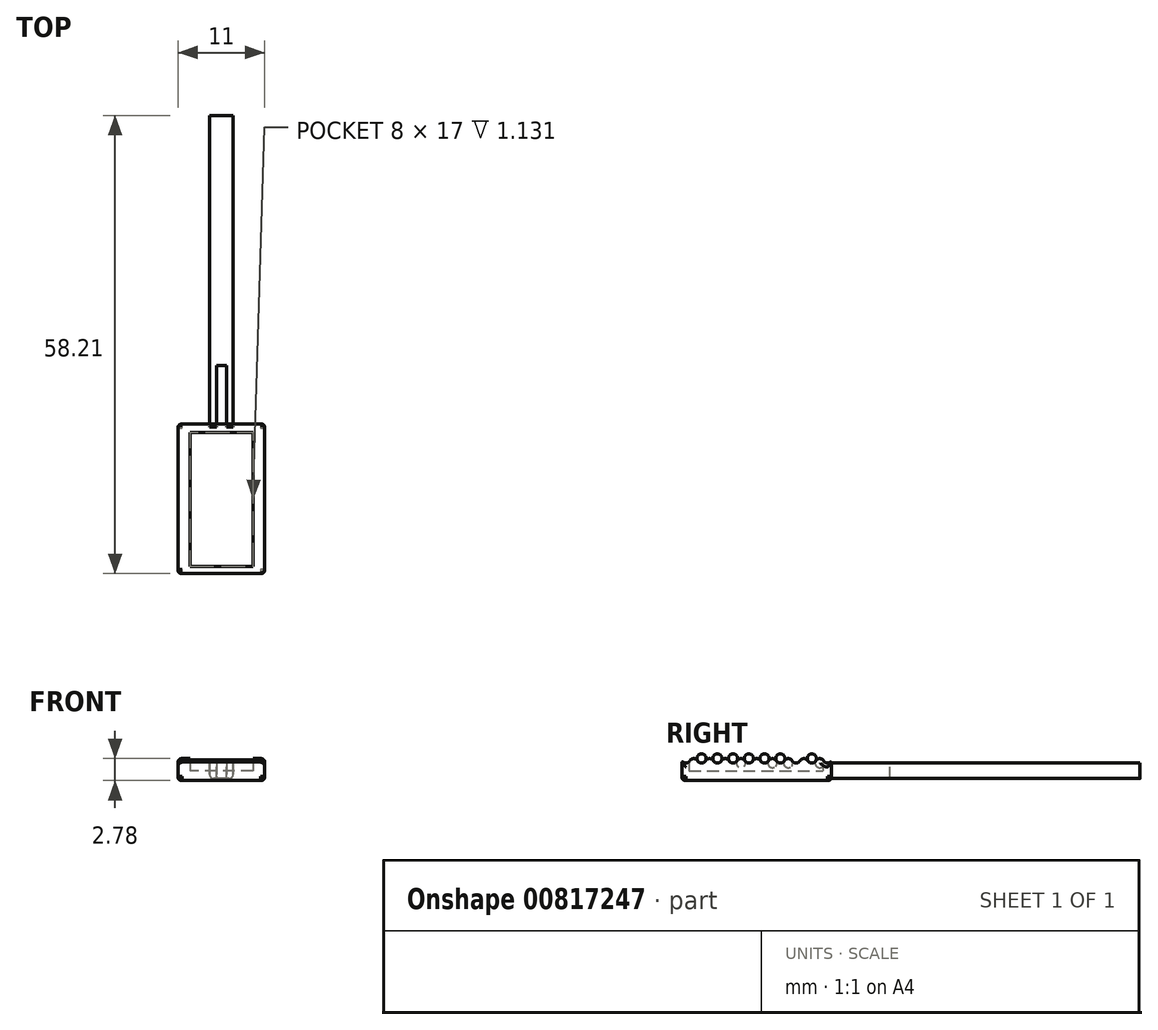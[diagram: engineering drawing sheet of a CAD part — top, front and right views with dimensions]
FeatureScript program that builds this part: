
annotation { "Feature Type Name" : "Feature", "Feature Type Description" : "" }
export const myFeature = defineFeature(function(context is Context, id is Id, definition is map)
    precondition{}
    {
        {
            var Q0;
            Q0=qCreatedBy(makeId("Right.planeOp"),FACE);
            var sketch = newSketch(context, id + "F0", { "sketchPlane" : qUnion([Q0])});
            skLineSegment(sketch, "E0.bottom", {"start": v(9.6, -1.25) * mm, "end": v(-9.4, -1.25) * mm});
            skLineSegment(sketch, "E1", {"start": v(9.6, 1) * mm, "end": v(9.6, -1.25) * mm});
            skLineSegment(sketch, "E2", {"start": v(-9.4, 1.08) * mm, "end": v(-9.4, -1.25) * mm});
            skArc(sketch, "E3.MirrorCS", {"start": v(-8.4, 1.25) * mm, "mid": v(-8.83, 0.97) * mm, "end": v(-9.3, 1.12) * mm});
            skArc(sketch, "E4.MirrorCS", {"start": v(6.6, 1.25) * mm, "mid": v(6.1, 1.53) * mm, "end": v(5.6, 1.25) * mm});
            skArc(sketch, "E5.MirrorCS", {"start": v(-5.4, 1.25) * mm, "mid": v(-5.9, 1.53) * mm, "end": v(-6.4, 1.25) * mm});
            skArc(sketch, "E6.MirrorCS", {"start": v(1.6, 1.25) * mm, "mid": v(1.1, 0.97) * mm, "end": v(0.6, 1.25) * mm});
            skArc(sketch, "E7.MirrorCS", {"start": v(-6.4, 1.25) * mm, "mid": v(-6.9, 0.97) * mm, "end": v(-7.4, 1.25) * mm});
            skArc(sketch, "E8.MirrorCS", {"start": v(8.6, 1.25) * mm, "mid": v(8.1, 1.53) * mm, "end": v(7.6, 1.25) * mm});
            skArc(sketch, "E9.MirrorCS", {"start": v(9.44, 1.08) * mm, "mid": v(8.98, 0.98) * mm, "end": v(8.6, 1.25) * mm});
            skArc(sketch, "E10.MirrorCS", {"start": v(-2.4, 1.25) * mm, "mid": v(-2.9, 0.97) * mm, "end": v(-3.4, 1.25) * mm});
            skArc(sketch, "E11.MirrorCS", {"start": v(-0.4, 1.25) * mm, "mid": v(-0.9, 0.97) * mm, "end": v(-1.4, 1.25) * mm});
            skArc(sketch, "E12.MirrorCS", {"start": v(-1.4, 1.25) * mm, "mid": v(-1.9, 1.53) * mm, "end": v(-2.4, 1.25) * mm});
            skArc(sketch, "E13.MirrorCS", {"start": v(2.6, 1.25) * mm, "mid": v(2.1, 1.53) * mm, "end": v(1.6, 1.25) * mm});
            skArc(sketch, "E14.MirrorCS", {"start": v(7.6, 1.25) * mm, "mid": v(7.1, 0.97) * mm, "end": v(6.6, 1.25) * mm});
            skArc(sketch, "E15.MirrorCS", {"start": v(3.6, 1.25) * mm, "mid": v(3.1, 0.97) * mm, "end": v(2.6, 1.25) * mm});
            skArc(sketch, "E16.MirrorCS", {"start": v(4.6, 1.25) * mm, "mid": v(4.1, 1.53) * mm, "end": v(3.6, 1.25) * mm});
            skArc(sketch, "E17.MirrorCS", {"start": v(-7.4, 1.25) * mm, "mid": v(-7.9, 1.53) * mm, "end": v(-8.4, 1.25) * mm});
            skArc(sketch, "E18.MirrorCS", {"start": v(-4.4, 1.25) * mm, "mid": v(-4.9, 0.97) * mm, "end": v(-5.4, 1.25) * mm});
            skArc(sketch, "E19.MirrorCS", {"start": v(5.6, 1.25) * mm, "mid": v(5.1, 0.97) * mm, "end": v(4.6, 1.25) * mm});
            skArc(sketch, "E20.MirrorCS", {"start": v(-3.4, 1.25) * mm, "mid": v(-3.9, 1.53) * mm, "end": v(-4.4, 1.25) * mm});
            skArc(sketch, "E21.MirrorCS", {"start": v(0.6, 1.25) * mm, "mid": v(0.1, 1.53) * mm, "end": v(-0.4, 1.25) * mm});
            skPoint(sketch, "E22.18.0.0.start.orphan", {"position": v(-8.4, 1.25) * mm});
            skPoint(sketch, "E22.16.0.0.end.orphan", {"position": v(-7.4, 1.25) * mm});
            skPoint(sketch, "E22.16.0.0.start.orphan", {"position": v(-6.4, 1.25) * mm});
            skPoint(sketch, "E23.18.0.0.center.orphan", {"position": v(9.1, 0.95) * mm});
            skPoint(sketch, "E23.18.0.0.end.orphan", {"position": v(8.6, 1.25) * mm});
            skArc(sketch, "E24.filletArc", {"start": v(9.6, 1) * mm, "mid": v(9.54, 1.09) * mm, "end": v(9.44, 1.08) * mm});
            skArc(sketch, "E25.filletArc", {"start": v(-9.3, 1.12) * mm, "mid": v(-9.37, 1.14) * mm, "end": v(-9.4, 1.08) * mm});
            skSolve(sketch);
        }
        {
            var Q0;
            Q0=qSketchRegion(id+"F0",true);
            extrude(context, id + "F1", {"entities" : qUnion([Q0]), "depth" : 11 * mm, "offsetDistance" : 25 * mm});
        }
        {
            var Q0;
            Q0=qCreatedBy(makeId("Top.planeOp"),FACE);
            var sketch = newSketch(context, id + "F2", { "sketchPlane" : qUnion([Q0])});
            skLineSegment(sketch, "E26", {"start": v(0, 0) * mm, "end": v(11, 0) * mm});
            skLineSegment(sketch, "E27.bottom", {"start": v(9.5, -8.5) * mm, "end": v(1.5, -8.5) * mm});
            skLineSegment(sketch, "E27.top", {"start": v(9.5, 8.5) * mm, "end": v(1.5, 8.5) * mm});
            skLineSegment(sketch, "E27.left", {"start": v(9.5, -8.5) * mm, "end": v(9.5, 8.5) * mm});
            skLineSegment(sketch, "E27.right", {"start": v(1.5, -8.5) * mm, "end": v(1.5, 8.5) * mm});
            skPoint(sketch, "E27.middle", {"position": v(5.5, 0) * mm});
            skSolve(sketch);
        }
        {
            var Q0;
            Q0=qSketchRegion(id+"F2",true);
            extrude(context, id + "F3", {"entities" : qUnion([Q0]), "operationType" : NewBodyOperationType.REMOVE, "endBound" : BoundingType.THROUGH_ALL, "depth" : 25 * mm, "offsetDistance" : 25 * mm});
        }
        {
            var Q0;
            Q0=qCreatedBy(makeId("Top.planeOp"),FACE);
            var sketch = newSketch(context, id + "F4", { "sketchPlane" : qUnion([Q0])});
            skLineSegment(sketch, "E28.top", {"start": v(7, 48.8) * mm, "end": v(4, 48.8) * mm});
            skLineSegment(sketch, "E28.left", {"start": v(7, 9.25) * mm, "end": v(7, 48.8) * mm});
            skLineSegment(sketch, "E28.right", {"start": v(4, 9.25) * mm, "end": v(4, 48.8) * mm});
            skPoint(sketch, "E28.middle", {"position": v(5.5, 29.02) * mm});
            skLineSegment(sketch, "E29.top", {"start": v(6.2, 17) * mm, "end": v(4.9, 17) * mm});
            skLineSegment(sketch, "E29.left", {"start": v(6.2, 9.25) * mm, "end": v(6.2, 17) * mm});
            skLineSegment(sketch, "E29.right", {"start": v(4.9, 9.25) * mm, "end": v(4.9, 17) * mm});
            skLineSegment(sketch, "E30.trimOffspring", {"start": v(4.9, 9.25) * mm, "end": v(4, 9.25) * mm});
            skLineSegment(sketch, "E31", {"start": v(6.2, 9.25) * mm, "end": v(7, 9.25) * mm});
            skSolve(sketch);
        }
        {
            var Q0;
            Q0 = qSketchRegion(id + "F4", true);
            extrude(context, id + "F5", {"entities" : qUnion([Q0]), "operationType" : NewBodyOperationType.ADD, "oppositeDirection" : true, "depth" : 1 * mm, "offsetDistance" : 25 * mm});
        }
        {
            var Q0;
            Q0 = qSketchRegion(id + "F4", true);
            extrude(context, id + "F6", {"entities" : qUnion([Q0]), "operationType" : NewBodyOperationType.ADD, "depth" : 1 * mm, "offsetDistance" : 25 * mm});
        }
        {
            var Q0;
            Q0=makeQuery(id+"F1.opExtrude","SWEPT_FACE",FACE,{"disambiguationData":[OSD([sQuery(id+"F0.wireOp",EDGE,"E0.bottom")])]});
            var Q1;
            Q1=makeQuery(id+"F1.opExtrude","CAP_FACE",FACE,{"disambiguationData":[OSD([sQuery(id+"F0.wireOp",EDGE,"E0.bottom"),sQuery(id+"F0.wireOp",EDGE,"E1"),sQuery(id+"F0.wireOp",EDGE,"E2"),sQuery(id+"F0.wireOp",EDGE,"E3.MirrorCS"),sQuery(id+"F0.wireOp",EDGE,"E4.MirrorCS"),sQuery(id+"F0.wireOp",EDGE,"E5.MirrorCS"),sQuery(id+"F0.wireOp",EDGE,"E6.MirrorCS"),sQuery(id+"F0.wireOp",EDGE,"E7.MirrorCS"),sQuery(id+"F0.wireOp",EDGE,"E8.MirrorCS"),sQuery(id+"F0.wireOp",EDGE,"E9.MirrorCS"),sQuery(id+"F0.wireOp",EDGE,"E10.MirrorCS"),sQuery(id+"F0.wireOp",EDGE,"E11.MirrorCS"),sQuery(id+"F0.wireOp",EDGE,"E12.MirrorCS"),sQuery(id+"F0.wireOp",EDGE,"E13.MirrorCS"),sQuery(id+"F0.wireOp",EDGE,"E14.MirrorCS"),sQuery(id+"F0.wireOp",EDGE,"E15.MirrorCS"),sQuery(id+"F0.wireOp",EDGE,"E16.MirrorCS"),sQuery(id+"F0.wireOp",EDGE,"E17.MirrorCS"),sQuery(id+"F0.wireOp",EDGE,"E18.MirrorCS"),sQuery(id+"F0.wireOp",EDGE,"E19.MirrorCS"),sQuery(id+"F0.wireOp",EDGE,"E20.MirrorCS"),sQuery(id+"F0.wireOp",EDGE,"E21.MirrorCS"),sQuery(id+"F0.wireOp",EDGE,"E24.filletArc"),sQuery(id+"F0.wireOp",EDGE,"E25.filletArc")])],"isStart":false});
            var Q2;
            Q2=makeQuery(id+"F1.opExtrude","CAP_FACE",FACE,{"disambiguationData":[OSD([sQuery(id+"F0.wireOp",EDGE,"E0.bottom"),sQuery(id+"F0.wireOp",EDGE,"E1"),sQuery(id+"F0.wireOp",EDGE,"E2"),sQuery(id+"F0.wireOp",EDGE,"E3.MirrorCS"),sQuery(id+"F0.wireOp",EDGE,"E4.MirrorCS"),sQuery(id+"F0.wireOp",EDGE,"E5.MirrorCS"),sQuery(id+"F0.wireOp",EDGE,"E6.MirrorCS"),sQuery(id+"F0.wireOp",EDGE,"E7.MirrorCS"),sQuery(id+"F0.wireOp",EDGE,"E8.MirrorCS"),sQuery(id+"F0.wireOp",EDGE,"E9.MirrorCS"),sQuery(id+"F0.wireOp",EDGE,"E10.MirrorCS"),sQuery(id+"F0.wireOp",EDGE,"E11.MirrorCS"),sQuery(id+"F0.wireOp",EDGE,"E12.MirrorCS"),sQuery(id+"F0.wireOp",EDGE,"E13.MirrorCS"),sQuery(id+"F0.wireOp",EDGE,"E14.MirrorCS"),sQuery(id+"F0.wireOp",EDGE,"E15.MirrorCS"),sQuery(id+"F0.wireOp",EDGE,"E16.MirrorCS"),sQuery(id+"F0.wireOp",EDGE,"E17.MirrorCS"),sQuery(id+"F0.wireOp",EDGE,"E18.MirrorCS"),sQuery(id+"F0.wireOp",EDGE,"E19.MirrorCS"),sQuery(id+"F0.wireOp",EDGE,"E20.MirrorCS"),sQuery(id+"F0.wireOp",EDGE,"E21.MirrorCS"),sQuery(id+"F0.wireOp",EDGE,"E24.filletArc"),sQuery(id+"F0.wireOp",EDGE,"E25.filletArc")])],"isStart":true});
            fillet(context, id + "F7", {"entities" : qUnion([Q0, Q1, Q2]), "radius" : .5 * mm, "tangentPropagation" : true, "rho" : 0.5, "crossSection" : FilletCrossSection.CONIC, "allowEdgeOverflow" : false});
        }
        {
            var Q0;
            Q0=makeQuery(id+"F5.opExtrude","CAP_EDGE",EDGE,{"disambiguationData":[OSD([sQuery(id+"F4.wireOp",EDGE,"E28.right")])],"isStart":false});
            var Q1;
            Q1=makeQuery(id+"F5.opExtrude","CAP_EDGE",EDGE,{"disambiguationData":[OSD([sQuery(id+"F4.wireOp",EDGE,"E28.left")])],"isStart":false});
            fillet(context, id + "F8", {"entities" : qUnion([Q0, Q1]), "radius" : .5 * mm, "tangentPropagation" : true, "allowEdgeOverflow" : false});
        }
    });
